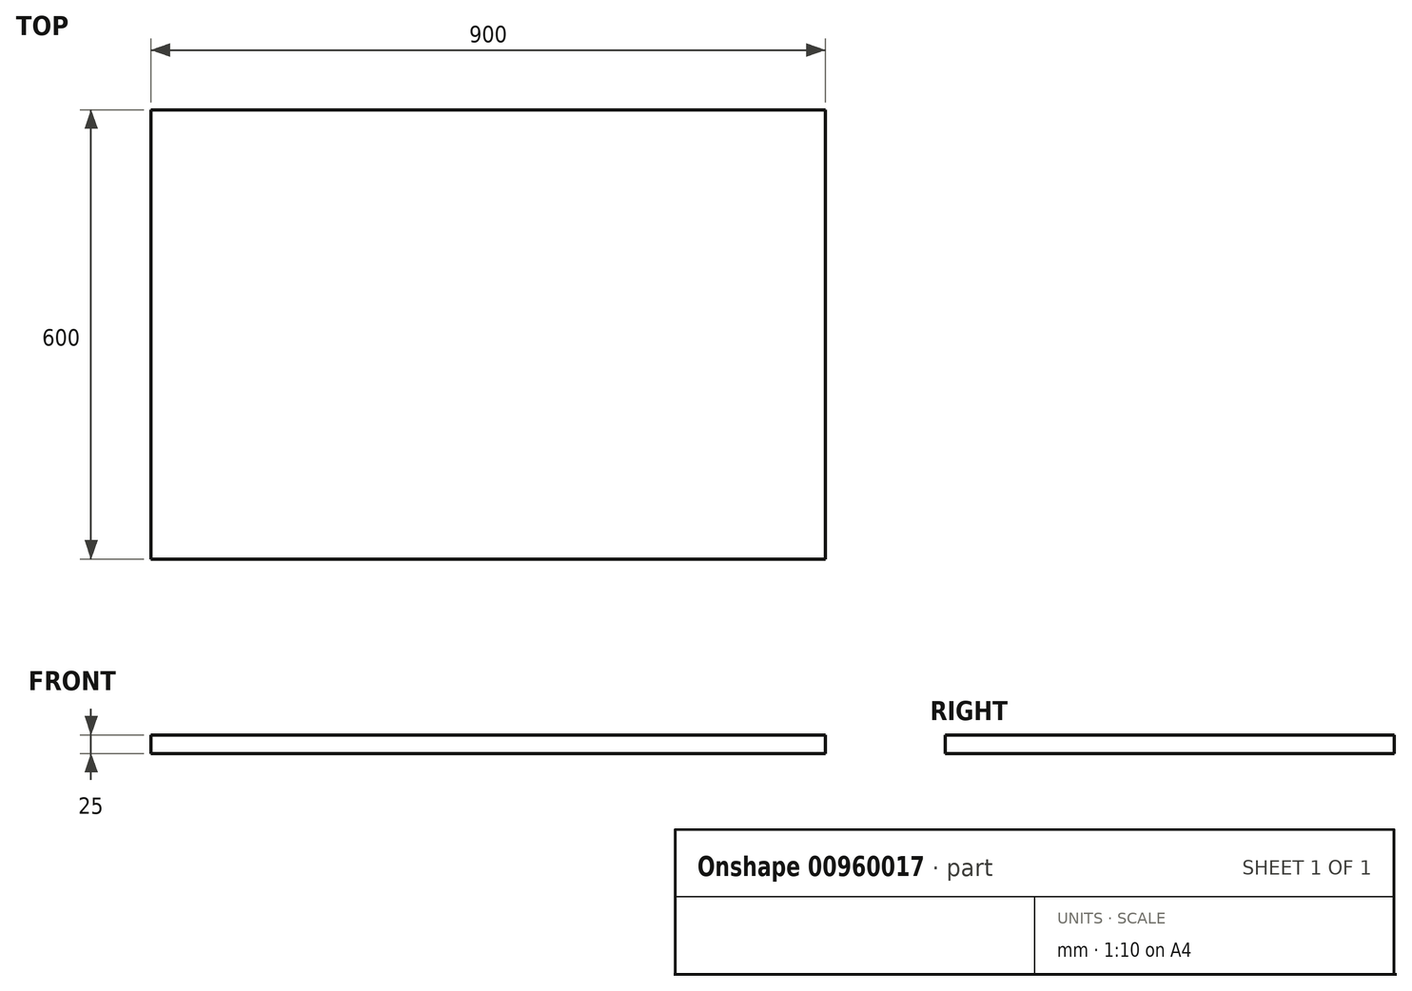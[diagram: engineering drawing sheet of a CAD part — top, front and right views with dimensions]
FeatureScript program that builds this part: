
annotation { "Feature Type Name" : "Feature", "Feature Type Description" : "" }
export const myFeature = defineFeature(function(context is Context, id is Id, definition is map)
    precondition{}
    {
        {
            var Q0;
            Q0=qCreatedBy(makeId("Top.planeOp"),FACE);
            var sketch = newSketch(context, id + "F0", { "sketchPlane" : qUnion([Q0])});
            skLineSegment(sketch, "E0.bottom", {"start": v(-390.11, 234.74) * mm, "end": v(509.89, 234.74) * mm});
            skLineSegment(sketch, "E0.top", {"start": v(-390.11, -365.26) * mm, "end": v(509.89, -365.26) * mm});
            skLineSegment(sketch, "E0.left", {"start": v(-390.11, 234.74) * mm, "end": v(-390.11, -365.26) * mm});
            skLineSegment(sketch, "E0.right", {"start": v(509.89, 234.74) * mm, "end": v(509.89, -365.26) * mm});
            skSolve(sketch);
        }
        {
            var Q0;
            Q0=makeQuery(id+"F0.imprint","IMPRINT",FACE,{"disambiguationData":[TD([[makeQuery(id+"F0.imprint","IMPRINT",EDGE,{"derivedFrom":sQuery(id+"F0.wireOp",EDGE,"E0.bottom")}),-1.0]])]});
            extrude(context, id + "F1", {"entities" : qUnion([Q0]), "depth" : 25 * mm, "offsetDistance" : 25 * mm});
        }
    });
